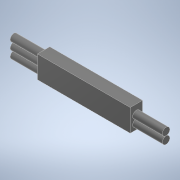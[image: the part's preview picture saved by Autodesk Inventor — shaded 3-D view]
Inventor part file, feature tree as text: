
AUTODESK INVENTOR PART (.ipt)
format: ipt  version: 2022 (Build 260153000, 153)  size: 120,320 bytes
history: native  units: in
note: dims shown in document units (in); Inventor stores cm internally (conversion verified against a paired STEP export)
features: extrude x3, sketch x2
ambient origin geometry x8: Origin, YZ Plane, XZ Plane, XY Plane, X Axis, Y Axis, Z Axis, Center Point
bodies: Solid1 (feature_tree)
feature tree (5):
  extrude  "Extrusion1"  Depth=0.3543in
  extrude  "Extrusion2"  Depth=0.4724in
  extrude  "Extrusion3"  Depth=0.4724in TaperAngle=0.0deg
  sketch  "Sketch1"  dims[d0=1.4764in d1=0.3543in]
  sketch  "Sketch3"  dims[d2=0.1969in d3=0.0in d4=0.1181in d7=0.4724in d8=0.0in d11=0.1181in d12=0.4724in d13=0.0in]
